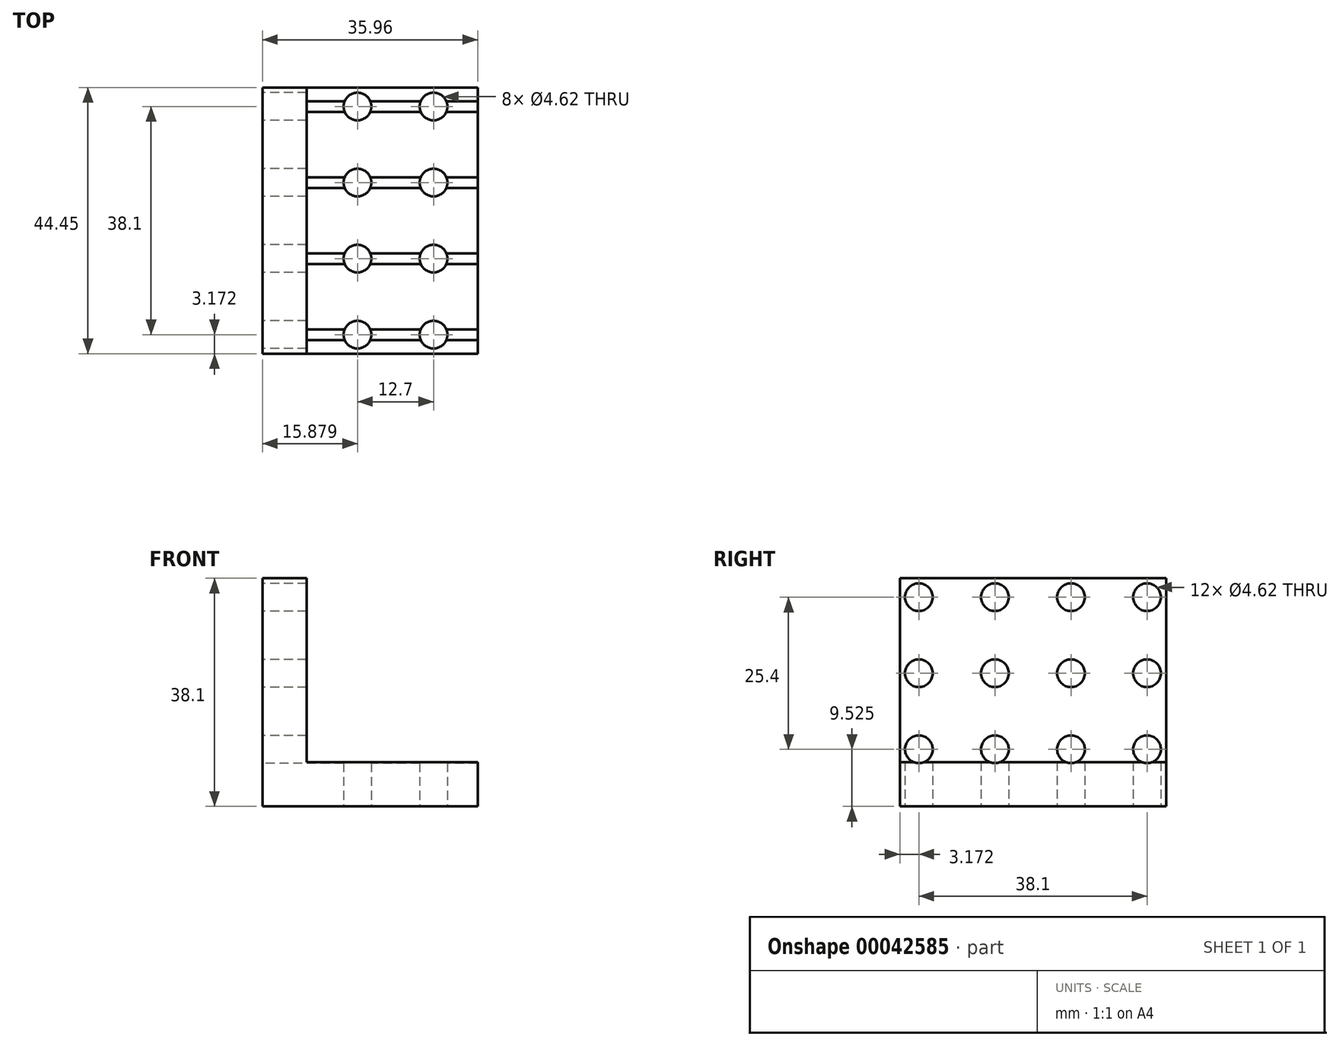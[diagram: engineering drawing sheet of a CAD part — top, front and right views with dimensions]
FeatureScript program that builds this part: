
annotation { "Feature Type Name" : "Feature", "Feature Type Description" : "" }
export const myFeature = defineFeature(function(context is Context, id is Id, definition is map)
    precondition{}
    {
        {
            var Q0;
            Q0=qCreatedBy(makeId("Top.planeOp"),FACE);
            var sketch = newSketch(context, id + "F0", { "sketchPlane" : qUnion([Q0])});
            skLineSegment(sketch, "E0.bottom", {"start": v(-30.35, 32.97) * mm, "end": v(5.61, 32.97) * mm});
            skLineSegment(sketch, "E0.top", {"start": v(-30.35, -11.48) * mm, "end": v(-22.95, -11.48) * mm});
            skLineSegment(sketch, "E0.left", {"start": v(-30.35, 32.97) * mm, "end": v(-30.35, -11.48) * mm});
            skCircle(sketch, "E1.1.0.0", {"center": v(-14.47, 17.1) * mm, "radius": 2.31 * mm});
            skCircle(sketch, "E1.1.1.0", {"center": v(-14.47, 4.4) * mm, "radius": 2.31 * mm});
            skCircle(sketch, "E1.1.2.0", {"center": v(-14.47, -8.3) * mm, "radius": 2.31 * mm});
            skCircle(sketch, "E1.2.0.0", {"center": v(-1.77, 17.1) * mm, "radius": 2.31 * mm});
            skCircle(sketch, "E1.2.1.0", {"center": v(-1.77, 4.4) * mm, "radius": 2.31 * mm});
            skCircle(sketch, "E1.2.2.0", {"center": v(-1.77, -8.3) * mm, "radius": 2.31 * mm});
            skLineSegment(sketch, "E2", {"start": v(-22.95, 32.97) * mm, "end": v(-22.95, -11.48) * mm});
            skLineSegment(sketch, "E3", {"start": v(5.61, 32.97) * mm, "end": v(5.61, -11.48) * mm});
            skCircle(sketch, "E4.0.1.0", {"center": v(-14.47, 29.8) * mm, "radius": 2.31 * mm});
            skCircle(sketch, "E5.0.1.0", {"center": v(-1.77, 29.8) * mm, "radius": 2.31 * mm});
            skLineSegment(sketch, "E6", {"start": v(5.61, -11.48) * mm, "end": v(-22.95, -11.48) * mm});
            skSolve(sketch);
        }
        {
            var Q0;
            {var subQ1=sQuery(id+"F0.wireOp",EDGE,"E0.left");Q0=makeQuery(id+"F0.imprint","IMPRINT",FACE,{"disambiguationData":[TD([[makeQuery(id+"F0.imprint","IMPRINT",EDGE,{"derivedFrom":subQ1}),1.0]])]});}
            extrude(context, id + "F1", {"entities" : qUnion([Q0]), "depth" : 38.1 * mm});
        }
        {
            var Q0;
            Q0=makeQuery(id+"F0.imprint","IMPRINT",FACE,{"disambiguationData":[TD([[makeQuery(id+"F0.imprint","IMPRINT",EDGE,{"derivedFrom":sQuery(id+"F0.wireOp",EDGE,"E1.1.0.0")}),-1.0]])]});
            extrude(context, id + "F2", {"entities" : qUnion([Q0]), "operationType" : NewBodyOperationType.ADD, "depth" : 7.4 * mm});
        }
        {
            var Q0;
            Q0=makeQuery(id+"F1.opExtrude","SWEPT_FACE",FACE,{"disambiguationData":[OSD([sQuery(id+"F0.wireOp",EDGE,"E0.left")])]});
            var sketch = newSketch(context, id + "F3", { "sketchPlane" : qUnion([Q0])});
            skCircle(sketch, "E7", {"center": v(-29.8, 34.93) * mm, "radius": 2.31 * mm});
            skCircle(sketch, "E8.0.1.0", {"center": v(-29.8, 22.23) * mm, "radius": 2.31 * mm});
            skCircle(sketch, "E8.0.2.0", {"center": v(-29.8, 9.52) * mm, "radius": 2.31 * mm});
            skCircle(sketch, "E8.1.0.0", {"center": v(-17.1, 34.93) * mm, "radius": 2.31 * mm});
            skCircle(sketch, "E8.1.1.0", {"center": v(-17.1, 22.23) * mm, "radius": 2.31 * mm});
            skCircle(sketch, "E8.1.2.0", {"center": v(-17.1, 9.52) * mm, "radius": 2.31 * mm});
            skCircle(sketch, "E8.2.0.0", {"center": v(-4.4, 34.93) * mm, "radius": 2.31 * mm});
            skCircle(sketch, "E8.2.1.0", {"center": v(-4.4, 22.23) * mm, "radius": 2.31 * mm});
            skCircle(sketch, "E8.2.2.0", {"center": v(-4.4, 9.52) * mm, "radius": 2.31 * mm});
            skCircle(sketch, "E8.3.0.0", {"center": v(8.3, 34.93) * mm, "radius": 2.31 * mm});
            skCircle(sketch, "E8.3.1.0", {"center": v(8.3, 22.23) * mm, "radius": 2.31 * mm});
            skCircle(sketch, "E8.3.2.0", {"center": v(8.3, 9.52) * mm, "radius": 2.31 * mm});
            skSolve(sketch);
        }
        {
            var Q0;
            Q0=makeQuery(id+"F3.imprint","IMPRINT",FACE,{"disambiguationData":[TD([[makeQuery(id+"F3.imprint","IMPRINT",EDGE,{"derivedFrom":sQuery(id+"F3.wireOp",EDGE,"E8.3.0.0")}),1.0]])]});
            var Q1;
            Q1=makeQuery(id+"F3.imprint","IMPRINT",FACE,{"disambiguationData":[TD([[makeQuery(id+"F3.imprint","IMPRINT",EDGE,{"derivedFrom":sQuery(id+"F3.wireOp",EDGE,"E8.2.0.0")}),1.0]])]});
            var Q2;
            Q2=makeQuery(id+"F3.imprint","IMPRINT",FACE,{"disambiguationData":[TD([[makeQuery(id+"F3.imprint","IMPRINT",EDGE,{"derivedFrom":sQuery(id+"F3.wireOp",EDGE,"E8.1.0.0")}),1.0]])]});
            var Q3;
            Q3=makeQuery(id+"F3.imprint","IMPRINT",FACE,{"disambiguationData":[TD([[makeQuery(id+"F3.imprint","IMPRINT",EDGE,{"derivedFrom":sQuery(id+"F3.wireOp",EDGE,"E7")}),1.0]])]});
            var Q4;
            Q4=makeQuery(id+"F3.imprint","IMPRINT",FACE,{"disambiguationData":[TD([[makeQuery(id+"F3.imprint","IMPRINT",EDGE,{"derivedFrom":sQuery(id+"F3.wireOp",EDGE,"E8.0.1.0")}),1.0]])]});
            var Q5;
            Q5=makeQuery(id+"F3.imprint","IMPRINT",FACE,{"disambiguationData":[TD([[makeQuery(id+"F3.imprint","IMPRINT",EDGE,{"derivedFrom":sQuery(id+"F3.wireOp",EDGE,"E8.1.1.0")}),1.0]])]});
            var Q6;
            Q6=makeQuery(id+"F3.imprint","IMPRINT",FACE,{"disambiguationData":[TD([[makeQuery(id+"F3.imprint","IMPRINT",EDGE,{"derivedFrom":sQuery(id+"F3.wireOp",EDGE,"E8.2.1.0")}),1.0]])]});
            var Q7;
            Q7=makeQuery(id+"F3.imprint","IMPRINT",FACE,{"disambiguationData":[TD([[makeQuery(id+"F3.imprint","IMPRINT",EDGE,{"derivedFrom":sQuery(id+"F3.wireOp",EDGE,"E8.3.1.0")}),1.0]])]});
            var Q8;
            Q8=makeQuery(id+"F3.imprint","IMPRINT",FACE,{"disambiguationData":[TD([[makeQuery(id+"F3.imprint","IMPRINT",EDGE,{"derivedFrom":sQuery(id+"F3.wireOp",EDGE,"E8.3.2.0")}),1.0]])]});
            var Q9;
            Q9=makeQuery(id+"F3.imprint","IMPRINT",FACE,{"disambiguationData":[TD([[makeQuery(id+"F3.imprint","IMPRINT",EDGE,{"derivedFrom":sQuery(id+"F3.wireOp",EDGE,"E8.2.2.0")}),1.0]])]});
            var Q10;
            Q10=makeQuery(id+"F3.imprint","IMPRINT",FACE,{"disambiguationData":[TD([[makeQuery(id+"F3.imprint","IMPRINT",EDGE,{"derivedFrom":sQuery(id+"F3.wireOp",EDGE,"E8.1.2.0")}),1.0]])]});
            var Q11;
            Q11=makeQuery(id+"F3.imprint","IMPRINT",FACE,{"disambiguationData":[TD([[makeQuery(id+"F3.imprint","IMPRINT",EDGE,{"derivedFrom":sQuery(id+"F3.wireOp",EDGE,"E8.0.2.0")}),1.0]])]});
            var Q12;
            Q12=sQuery(id+"F3.wireOp",EDGE,"E7");
            var Q13;
            Q13=sQuery(id+"F3.wireOp",EDGE,"E8.1.0.0");
            var Q14;
            Q14=sQuery(id+"F3.wireOp",EDGE,"E8.2.0.0");
            var Q15;
            Q15=sQuery(id+"F3.wireOp",EDGE,"E8.3.0.0");
            var Q16;
            Q16=sQuery(id+"F3.wireOp",EDGE,"E8.3.1.0");
            var Q17;
            Q17=sQuery(id+"F3.wireOp",EDGE,"E8.2.1.0");
            var Q18;
            Q18=sQuery(id+"F3.wireOp",EDGE,"E8.1.1.0");
            var Q19;
            Q19=sQuery(id+"F3.wireOp",EDGE,"E8.0.1.0");
            var Q20;
            Q20=sQuery(id+"F3.wireOp",EDGE,"E8.0.2.0");
            var Q21;
            Q21=sQuery(id+"F3.wireOp",EDGE,"E8.1.2.0");
            var Q22;
            Q22=sQuery(id+"F3.wireOp",EDGE,"E8.2.2.0");
            var Q23;
            Q23=sQuery(id+"F3.wireOp",EDGE,"E8.3.2.0");
            extrude(context, id + "F4", {"entities" : qUnion([Q0, Q1, Q2, Q3, Q4, Q5, Q6, Q7, Q8, Q9, Q10, Q11]), "operationType" : NewBodyOperationType.REMOVE, "surfaceEntities" : qUnion([Q12, Q13, Q14, Q15, Q16, Q17, Q18, Q19, Q20, Q21, Q22, Q23]), "oppositeDirection" : true, "depth" : 50.8 * mm});
        }
    });
